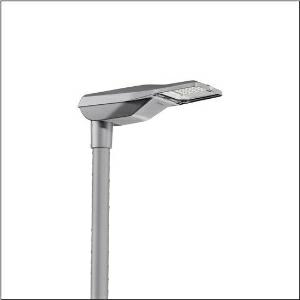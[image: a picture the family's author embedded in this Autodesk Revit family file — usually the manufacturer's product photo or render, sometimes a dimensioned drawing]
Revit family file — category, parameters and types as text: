
# Revit family: streetlight_sl_21_iq_micro___st0_8a_5xe1c41d08cb_e31f
name_source: partatom
category: Lighting Fixtures
units: mm (PartAtom-declared; Revit-internal decimal feet)

## family parameters
Cut with Voids When Loaded = No
Host = Face
Light Source = No
Part Type = Normal
Room Calculation Point = No
Round Connector Dimension = Use Diameter
Shared = No

## types (1)
- --- (1 x LED, 2980 lm, 19.4 W, 4000K)
    Apparent Load = 19 VA
    CIE Flux Codes = 38 75 97 100 100
    Color Rendering = 70
    Color Temperature = 4000K
    Default Elevation = 1800 mm
    Description = Streetlight SL 21 iQ micro, mast luminaire, primary light control with lens, of PMMA, primary optical cover: cover, of toughened safety glass, transparent, light distribution: ST0.8a, light emission: direct distribution, primary light characteristic: asymmetric, installation type: post-top, side-entry, LED, High Power LED, rated luminous flux: 2.980lm, luminous efficacy: 154lm/W, light colour: 740, colour temperature: 4000K, control gear: iQ-Comfort, control: Auto-Match, Temp-Guard, Lumen-Switch, Night-Set, Smart-Wire, Light-Fading, Desk-Remote (wireless, voltage-free reading and setting of iQ features in the workshop via application-optimized NFC function/RFID function), optimised constant luminous flux control (CLO 2.0), pre-setting: linear dimming characteristic, mains connection: 220..240V, AC, 50/60Hz, start of lifetime: 19W, end of service life: 20W, reduction: 10W, luminaire housing, of diecast aluminium, powder-coated, SITECO metallic grey (DB 702S), corrosivity category C5 high according to DIN EN ISO 12944, please order mast flange separately, inclination adjustable: 0°, 5°, 10°, 15°, sealing non-destructively replaceable, multi-level sealing system, length: 528mm, width: 235mm, height: 110mm, mast flange for spigot size: 42mm (side-entry): 5XC10008XM4, 60/48mm (side-entry/post-top): 5XC10108XM2, 76/60mm (side-entry/post-top): 5XC10108XM1, protection rating (complete): IP66, insulation class (complete): insulation class II (safety insulation), certification: CE, ENEC, ENEC+, VDE, impact resistance: IK10, permissible operating ambient temperature for outdoor applications: -40..+50°C, standard-compliant lighting for roads and squares, packaging unit: 1 piece

Light Distribution: ST0.8a
    Height = 110 mm
    Lamp = 1 x LED
    Lamp Light Flux = 2980 lm
    Lamp Power = 19.4 W
    Lamp count = 1
    Length = 528 mm
    Luminous efficacy = 154 lm/W
    Manufacturer = Siteco
    ModVariant = No
    Model = 5XE1C41D08CB
    Number of Poles = 1
    OnlyDefault = Yes
    Power Factor = 1
    Product Name = Streetlight SL 21 iQ micro | ST0.8a
    Product group = mast luminaire | pylon top
    ProductGroupID = 6100
    Protection Class = Protection class II
    Protection Degree = IP 66
    RLX_Detail_Level = 1
    RLX_Emergency_Light_Flux = 0 lm
    RLX_Emergency_Type = 0
    RLX_Emergency_Type_DB = No
    RlxData = <blob elided: 98325 chars, md5=c257a571>
    Socket = socket
    Standby Power = 0 W
    System Light Flux = 2980 lm
    System Power = 19 W
    Type Comments = factory setting: luminous flux: 100 % | dim-lin: 254 | 387 mA
    Type Image = l_1006881.jpg
    URL = http://relux.com
    VarID = @adj_137887
    Voltage = 0 V
    Weight = 0.00 kg
    Width = 235 mm

## geometry (parser evidence)
native form markers: Blend x4, Sweep x11
no freeform markers — native parametric forms only
